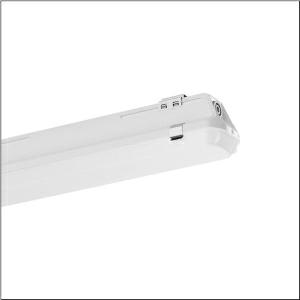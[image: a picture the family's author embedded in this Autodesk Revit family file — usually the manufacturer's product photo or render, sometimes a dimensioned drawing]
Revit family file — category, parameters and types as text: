
# Revit family: monsun_r__11_chemical_51fp30mp480h_0948
name_source: partatom
category: Lighting Fixtures
units: mm (PartAtom-declared; Revit-internal decimal feet)

## family parameters
Cut with Voids When Loaded = No
Host = Face
Light Source = No
Part Type = Normal
Room Calculation Point = No
Round Connector Dimension = Use Diameter
Shared = No

## types (1)
- --- (1 x LED, 7640 lm, 45.4 W, 4000K)
    Apparent Load = 45 VA
    CIE Flux Codes = 48 77 93 95 100
    Color Rendering = 80
    Color Temperature = 4000K
    Default Elevation = 1800 mm
    Description = Monsun® 11 chemical, damp-proof luminaire, chain hanger, primary optical cover: enclosure, of PA, light emission: direct distribution, primary light characteristic: symmetric, installation type: suspended mounting, surface-mounted, horizontal mounting, vertical mounting, LED, rated luminous flux: 7.640lm, luminous efficacy: 168lm/W, light colour: 840, colour temperature: 4000K, control gear: ECG, with terminal, 3-pole, max. 2.5mm², mains connection: 220..240V, AC, 50/60Hz, rated input power: 45W, luminaire housing, of glass-fibre reinforced polyester, uncoated, bright grey, incl. chain hanger, length: 1.590mm, width: 90mm, height: 88mm, clip for enclosure, of stainless steel (V2A), ceiling mounting element, of stainless steel (V2A), chain hanger, of stainless steel (V2A), protection rating (complete): IP66, insulation class (complete): insulation class I (protective earthing), certification: CE, ENEC, VDE, UKCA, protection symbol: D, impact resistance: IK08, permissible operating ambient temperature: -35..+40°C, standard: EN 50419, EN 60598-2-1, no direct snow, no direct sun, no direct rain, for indoor or canopied outdoor use, corresponds to IFS (International Featured Standards) requirements for safety and quality in the food industry, contact your sales advisor before using the luminaires in applications with unclear chemical exposure, large temperature fluctuations or condensation-forming humidity, LABS conformity tested according to VDMA 24364:2018-05, packaging unit: 1 piece
    Height = 89 mm
    Lamp = 1 x LED
    Lamp Light Flux = 7640 lm
    Lamp Power = 45.4 W
    Lamp count = 1
    Length = 1590 mm
    Luminous efficacy = 168 lm/W
    Manufacturer = Siteco
    ModVariant = No
    Model = 51FP30MP480H
    Mounting Place = Ceiling
    Mounting Type = Surface mounted
    Number of Poles = 1
    OnlyDefault = Yes
    Power Factor = 1
    Product Name = Monsun® 11 chemical
    Product group = damp-proof luminaire
    ProductGroupID = 301
    Protection Class = Protection class I
    Protection Degree = IP 66
    RLX_Detail_Level = 1
    RLX_Emergency_Light_Flux = 0 lm
    RLX_Emergency_Type = 0
    RLX_Emergency_Type_DB = No
    RlxData = <blob elided: 90053 chars, md5=17323ecb>
    Socket = socket
    Standby Power = 0 W
    System Light Flux = 7640 lm
    System Power = 45 W
    Type Comments = factory setting: luminous flux: 100 % | (A | C | E) | 105 mA
    Type Image = l_1004748.jpg
    URL = http://relux.com
    VarID = @adj_157179
    Voltage = 0 V
    Weight = 0.00 kg
    Width = 90 mm

## geometry (parser evidence)
native form markers: Blend x4, Sweep x12
no freeform markers — native parametric forms only
